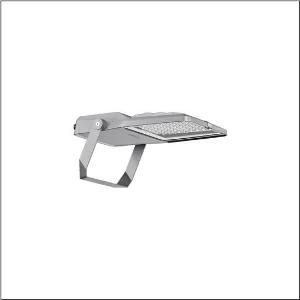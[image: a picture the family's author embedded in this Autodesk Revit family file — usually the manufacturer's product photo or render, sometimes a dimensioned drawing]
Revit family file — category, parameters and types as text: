
# Revit family: floodlight_fl_21_iq_mini___pl43_5xa7772d1a1a_00f7
name_source: partatom
category: Lighting Fixtures
units: mm (PartAtom-declared; Revit-internal decimal feet)

## family parameters
Cut with Voids When Loaded = No
Host = Face
Light Source = No
Part Type = Normal
Room Calculation Point = No
Round Connector Dimension = Use Diameter
Shared = No

## types (1)
- --- (1 x LED, 15140 lm, 143 W, 2200K)
    Apparent Load = 143 VA
    CIE Flux Codes = 27 78 99 100 100
    Color Rendering = 70
    Color Temperature = 2200K
    Default Elevation = 1800 mm
    Description = Floodlight FL 21 iQ mini, floodlight, primary light control with lens, of PMMA, primary optical cover: protective disc, of toughened safety glass, transparent, light distribution: PL43, light emission: direct distribution, installation type: surface-mounted, LED, High Power LED, rated luminous flux: 15.140lm, luminous efficacy: 106lm/W, light colour: 722, colour temperature: 2200K, control: Street-Remote, Auto-Match, Temp-Guard, Night-Set, Smart-Wire, Desk-Remote (wireless, voltage-free reading and setting of iQ features in the workshop via application-optimized NFC function/RFID function), optimised constant luminous flux control (CLO 2.0), with terminal, 6-pole, mains connection: 220..240V, AC, 50/60Hz, start of lifetime: 143W, end of service life: 152W, reduction: 61W, luminaire housing, of diecast aluminium, powder-coated, Siteco® metallic grey (DB 702S), corrosivity category C5 mid according to DIN EN ISO 12944, sealing non-destructively replaceable, mounting bracket, of steel, galvanised, powder-coated, Siteco® metallic grey (DB 702S), protection rating (complete): IP66, insulation class (complete): insulation class II (safety insulation), certification: CE, ENEC, VDE, protection symbol: D, impact resistance: IK08, permissible operating ambient temperature: -40..+40°C, permissible operating ambient temperature for outdoor applications: -40..+50°C, standard: DIN EN 12944, LABS conformity tested according to VDMA 24364:2018-05, packaging unit: 1 piece

Light Distribution: PL43
    Height = 70 mm
    Lamp = 1 x LED
    Lamp Light Flux = 15140 lm
    Lamp Power = 143 W
    Lamp count = 1
    Length = 485 mm
    Luminous efficacy = 106 lm/W
    Manufacturer = Siteco
    ModVariant = No
    Model = 5XA7772D1A1A
    Number of Poles = 1
    OnlyDefault = Yes
    Power Factor = 1
    Product Name = Floodlight FL 21 iQ mini | PL43
    Product group = floodlight | pylon annexe
    ProductGroupID = 6200
    Protection Class = Protection class II
    Protection Degree = IP 66
    RLX_Detail_Level = 1
    RLX_Emergency_Light_Flux = 0 lm
    RLX_Emergency_Type = 0
    RLX_Emergency_Type_DB = No
    RlxData = <blob elided: 96333 chars, md5=2725d6cd>
    Socket = socket
    Standby Power = 0 W
    System Light Flux = 15140 lm
    System Power = 143 W
    Type Comments = factory setting: luminous flux: 100 % | dim-lin: 254 | 730 mA
    Type Image = l_1006845.jpg
    URL = http://relux.com
    VarID = @adj_094015
    Voltage = 0 V
    Weight = 0.00 kg
    Width = 337 mm

## geometry (parser evidence)
native form markers: Blend x4, Sweep x11
no freeform markers — native parametric forms only
